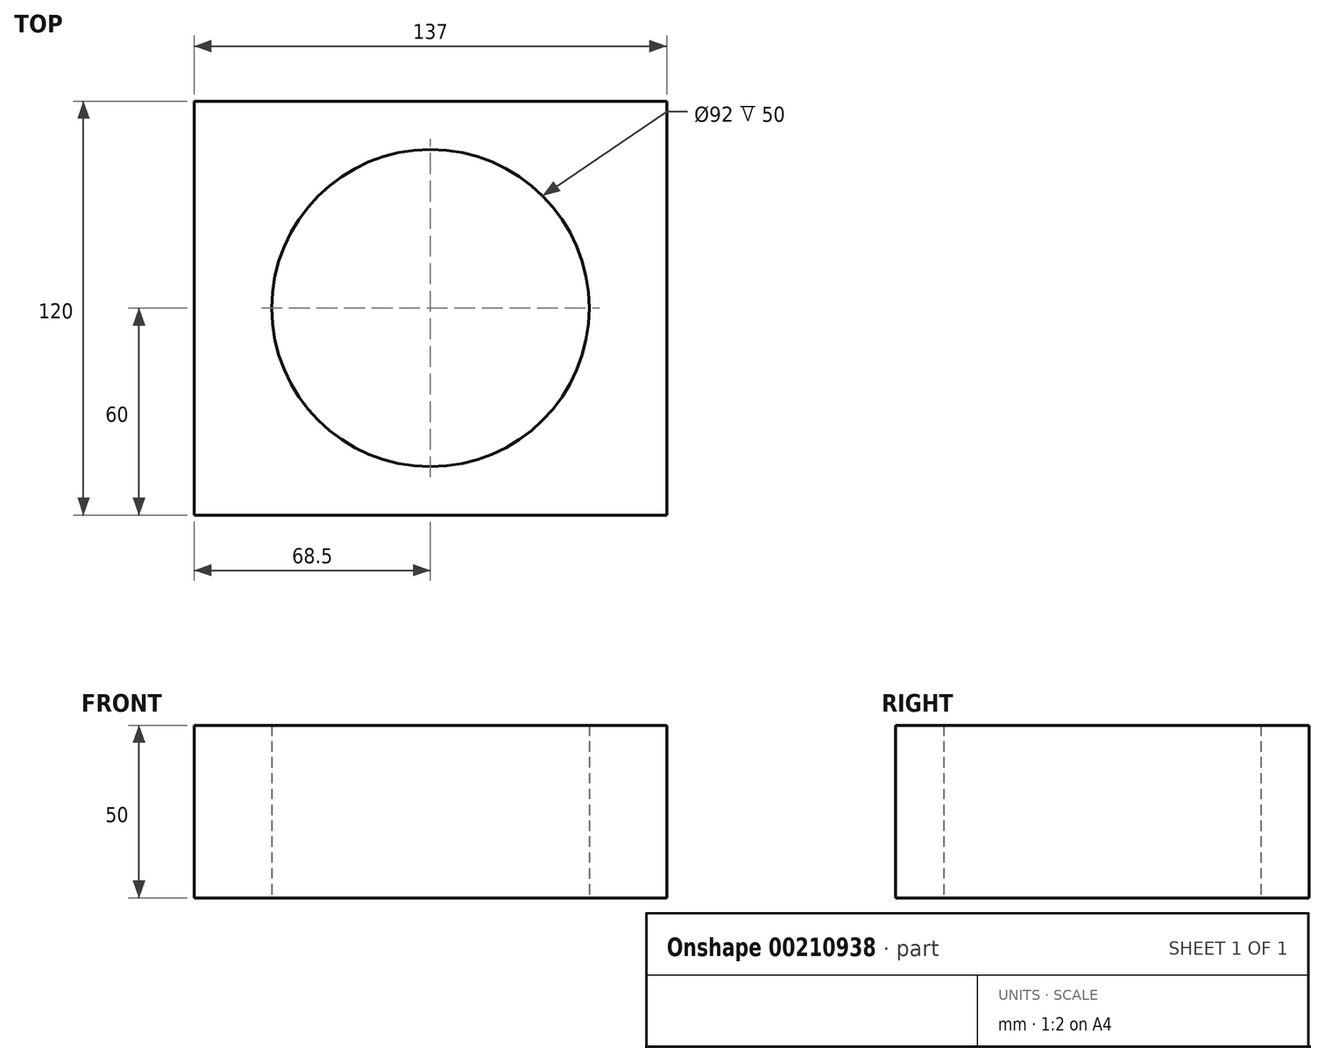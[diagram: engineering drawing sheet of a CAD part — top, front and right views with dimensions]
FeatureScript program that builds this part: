
annotation { "Feature Type Name" : "Feature", "Feature Type Description" : "" }
export const myFeature = defineFeature(function(context is Context, id is Id, definition is map)
    precondition{}
    {
        {
            var Q0;
            Q0=qCreatedBy(makeId("Top.planeOp"),FACE);
            var sketch = newSketch(context, id + "F0", { "sketchPlane" : qUnion([Q0])});
            skCircle(sketch, "E0", {"center": v(0, 0) * mm, "radius": 46 * mm});
            skLineSegment(sketch, "E1", {"start": v(0, 0) * mm, "end": v(61, 0) * mm});
            skLineSegment(sketch, "E2", {"start": v(61, 0) * mm, "end": v(68.5, 0) * mm});
            skLineSegment(sketch, "E3", {"start": v(68.5, 0) * mm, "end": v(68.5, -60) * mm});
            skLineSegment(sketch, "E4", {"start": v(68.5, -60) * mm, "end": v(0, -60) * mm});
            skLineSegment(sketch, "E5.MirrorCS", {"start": v(68.5, 0) * mm, "end": v(68.5, 60) * mm});
            skLineSegment(sketch, "E6.MirrorCS", {"start": v(68.5, 60) * mm, "end": v(0, 60) * mm});
            skLineSegment(sketch, "E7", {"start": v(0, 0) * mm, "end": v(0, 18.9) * mm});
            skLineSegment(sketch, "E8.MirrorCS", {"start": v(-68.5, 60) * mm, "end": v(0, 60) * mm});
            skLineSegment(sketch, "E9.MirrorCS", {"start": v(-68.5, 0) * mm, "end": v(-68.5, 60) * mm});
            skLineSegment(sketch, "E10.MirrorCS", {"start": v(-68.5, 0) * mm, "end": v(-68.5, -60) * mm});
            skLineSegment(sketch, "E11.MirrorCS", {"start": v(-68.5, -60) * mm, "end": v(0, -60) * mm});
            skSolve(sketch);
        }
        {
            var Q0;
            Q0 = qSketchRegion(id + "F0", true);
            extrude(context, id + "F1", {"entities" : qUnion([Q0]), "depth" : 50 * mm});
        }
    });
